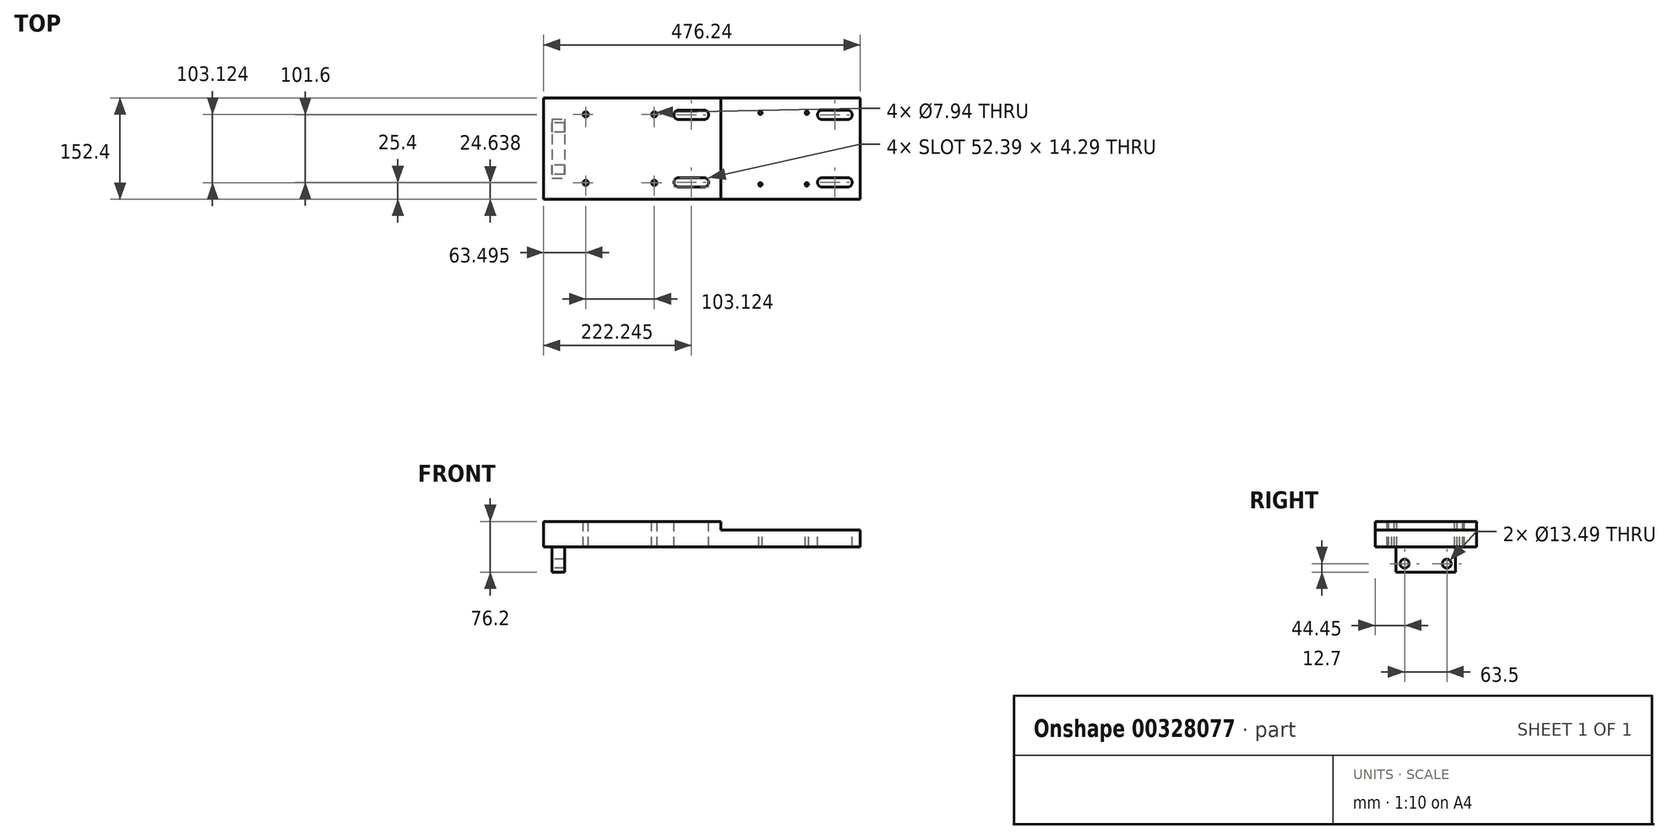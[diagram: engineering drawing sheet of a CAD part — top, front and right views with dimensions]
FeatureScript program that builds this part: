
annotation { "Feature Type Name" : "Feature", "Feature Type Description" : "" }
export const myFeature = defineFeature(function(context is Context, id is Id, definition is map)
    precondition{}
    {
        {
            var Q0;
            Q0=qCreatedBy(makeId("Top.planeOp"),FACE);
            var sketch = newSketch(context, id + "F0", { "sketchPlane" : qUnion([Q0])});
            skLineSegment(sketch, "E0.bottom", {"start": v(-238.13, 76.2) * mm, "end": v(238.13, 76.2) * mm});
            skLineSegment(sketch, "E0.top", {"start": v(-238.13, -76.2) * mm, "end": v(238.12, -76.2) * mm});
            skLineSegment(sketch, "E0.left", {"start": v(-238.13, 76.2) * mm, "end": v(-238.13, -76.2) * mm});
            skLineSegment(sketch, "E0.right", {"start": v(238.13, 76.2) * mm, "end": v(238.12, -76.2) * mm});
            skPoint(sketch, "E0.middle", {"position": v(0, 0) * mm});
            skSolve(sketch);
        }
        {
            var Q0;
            Q0 = qSketchRegion(id + "F0", true);
            extrude(context, id + "F1", {"entities" : qUnion([Q0]), "depth" : 38.1 * mm});
        }
        {
            var Q0;
            Q0=makeQuery(id+"F1.opExtrude","CAP_FACE",FACE,{"disambiguationData":[OSD([sQuery(id+"F0.wireOp",EDGE,"E0.bottom"),sQuery(id+"F0.wireOp",EDGE,"E0.top"),sQuery(id+"F0.wireOp",EDGE,"E0.left"),sQuery(id+"F0.wireOp",EDGE,"E0.right")])],"isStart":false});
            var sketch = newSketch(context, id + "F2", { "sketchPlane" : qUnion([Q0])});
            skPoint(sketch, "E1.0", {"position": v(238.12, -76.2) * mm});
            skLineSegment(sketch, "E2.bottom", {"start": v(238.12, -76.2) * mm, "end": v(28.57, -76.2) * mm});
            skLineSegment(sketch, "E2.top", {"start": v(238.12, 76.2) * mm, "end": v(28.57, 76.2) * mm});
            skLineSegment(sketch, "E2.left", {"start": v(238.12, -76.2) * mm, "end": v(238.12, 76.2) * mm});
            skLineSegment(sketch, "E2.right", {"start": v(28.57, -76.2) * mm, "end": v(28.57, 76.2) * mm});
            skSolve(sketch);
        }
        {
            var Q0;
            Q0 = qSketchRegion(id + "F2", true);
            extrude(context, id + "F3", {"entities" : qUnion([Q0]), "operationType" : NewBodyOperationType.REMOVE, "oppositeDirection" : true, "depth" : 12.7 * mm});
        }
        {
            var Q0;
            Q0=makeQuery(id+"F1.opExtrude","CAP_FACE",FACE,{"disambiguationData":[OSD([sQuery(id+"F0.wireOp",EDGE,"E0.bottom"),sQuery(id+"F0.wireOp",EDGE,"E0.top"),sQuery(id+"F0.wireOp",EDGE,"E0.left"),sQuery(id+"F0.wireOp",EDGE,"E0.right")])],"isStart":false});
            var sketch = newSketch(context, id + "F4", { "sketchPlane" : qUnion([Q0])});
            skLineSegment(sketch, "E3", {"start": v(-358.49, 0) * mm, "end": v(316.47, 0) * mm, "construction": true});
            skLineSegment(sketch, "E4.0", {"start": v(-34.93, 76.2) * mm, "end": v(-34.93, -76.2) * mm, "construction": true});
            skLineSegment(sketch, "E5.0", {"start": v(3.17, 76.2) * mm, "end": v(3.17, -76.2) * mm, "construction": true});
            skLineSegment(sketch, "E6.0", {"start": v(180.97, 76.2) * mm, "end": v(180.97, -76.2) * mm, "construction": true});
            skLineSegment(sketch, "E7.0", {"start": v(219.07, 76.2) * mm, "end": v(219.07, -76.2) * mm, "construction": true});
            skLineSegment(sketch, "E8.0", {"start": v(-358.49, -50.8) * mm, "end": v(316.47, -50.8) * mm, "construction": true});
            skArc(sketch, "E9", {"start": v(-34.93, -43.66) * mm, "mid": v(-42.07, -50.8) * mm, "end": v(-34.93, -57.94) * mm});
            skArc(sketch, "E10", {"start": v(3.17, -57.94) * mm, "mid": v(10.32, -50.8) * mm, "end": v(3.17, -43.66) * mm});
            skArc(sketch, "E11", {"start": v(180.97, -43.66) * mm, "mid": v(173.83, -50.8) * mm, "end": v(180.97, -57.94) * mm});
            skArc(sketch, "E12", {"start": v(219.07, -57.94) * mm, "mid": v(226.22, -50.8) * mm, "end": v(219.07, -43.66) * mm});
            skLineSegment(sketch, "E13", {"start": v(-34.93, -43.66) * mm, "end": v(3.17, -43.66) * mm});
            skLineSegment(sketch, "E14", {"start": v(-34.93, -57.94) * mm, "end": v(3.17, -57.94) * mm});
            skLineSegment(sketch, "E15", {"start": v(180.97, -43.66) * mm, "end": v(219.07, -43.66) * mm});
            skLineSegment(sketch, "E16", {"start": v(180.97, -57.94) * mm, "end": v(219.07, -57.94) * mm});
            skArc(sketch, "E17.MirrorCS", {"start": v(-34.93, 43.66) * mm, "mid": v(-42.07, 50.8) * mm, "end": v(-34.93, 57.94) * mm});
            skArc(sketch, "E18.MirrorCS", {"start": v(3.17, 57.94) * mm, "mid": v(10.32, 50.8) * mm, "end": v(3.17, 43.66) * mm});
            skLineSegment(sketch, "E19.MirrorCS", {"start": v(-34.93, 43.66) * mm, "end": v(3.17, 43.66) * mm});
            skLineSegment(sketch, "E20.MirrorCS", {"start": v(-34.93, 57.94) * mm, "end": v(3.17, 57.94) * mm});
            skLineSegment(sketch, "E21.MirrorCS", {"start": v(180.97, 43.66) * mm, "end": v(219.07, 43.66) * mm});
            skLineSegment(sketch, "E22.MirrorCS", {"start": v(180.97, 57.94) * mm, "end": v(219.07, 57.94) * mm});
            skArc(sketch, "E23.MirrorCS", {"start": v(180.97, 43.66) * mm, "mid": v(173.83, 50.8) * mm, "end": v(180.97, 57.94) * mm});
            skArc(sketch, "E24.MirrorCS", {"start": v(219.07, 57.94) * mm, "mid": v(226.22, 50.8) * mm, "end": v(219.07, 43.66) * mm});
            skSolve(sketch);
        }
        {
            var Q0;
            Q0 = qSketchRegion(id + "F4", true);
            extrude(context, id + "F5", {"entities" : qUnion([Q0]), "operationType" : NewBodyOperationType.REMOVE, "endBound" : BoundingType.THROUGH_ALL, "oppositeDirection" : true, "depth" : 25.4 * mm});
        }
        {
            var Q0;
            Q0=makeQuery(id+"F1.opExtrude","CAP_FACE",FACE,{"disambiguationData":[OSD([sQuery(id+"F0.wireOp",EDGE,"E0.bottom"),sQuery(id+"F0.wireOp",EDGE,"E0.top"),sQuery(id+"F0.wireOp",EDGE,"E0.left"),sQuery(id+"F0.wireOp",EDGE,"E0.right")])],"isStart":false});
            var sketch = newSketch(context, id + "F6", { "sketchPlane" : qUnion([Q0])});
            skLineSegment(sketch, "E25.0", {"start": v(-174.63, 76.2) * mm, "end": v(-174.63, -76.2) * mm, "construction": true});
            skLineSegment(sketch, "E26.0", {"start": v(-71.5, 76.2) * mm, "end": v(-71.5, -76.2) * mm, "construction": true});
            skLineSegment(sketch, "E27", {"start": v(-290.48, 0) * mm, "end": v(301.62, 0) * mm, "construction": true});
            skLineSegment(sketch, "E28.0", {"start": v(-290.48, -51.56) * mm, "end": v(-71.5, -51.56) * mm, "construction": true});
            skPoint(sketch, "E29", {"position": v(-174.63, -51.56) * mm});
            skPoint(sketch, "E30", {"position": v(-71.5, -51.56) * mm});
            skPoint(sketch, "E31.MirrorP", {"position": v(-174.63, 51.56) * mm});
            skPoint(sketch, "E32.MirrorP", {"position": v(-71.5, 51.56) * mm});
            skLineSegment(sketch, "E33.0", {"start": v(88.01, 76.2) * mm, "end": v(88.01, -76.2) * mm, "construction": true});
            skLineSegment(sketch, "E34.0", {"start": v(157.86, 76.2) * mm, "end": v(157.86, -76.2) * mm, "construction": true});
            skLineSegment(sketch, "E35.0", {"start": v(88.01, -53.85) * mm, "end": v(301.62, -53.85) * mm, "construction": true});
            skPoint(sketch, "E36", {"position": v(88.01, -53.85) * mm});
            skPoint(sketch, "E37", {"position": v(157.86, -53.85) * mm});
            skPoint(sketch, "E38.MirrorP", {"position": v(88.01, 53.85) * mm});
            skPoint(sketch, "E39.MirrorP", {"position": v(157.86, 53.85) * mm});
            skSolve(sketch);
        }
        {
            var Q0;
            Q0=sQuery(id+"F6.wireOp",VERTEX,"E31.MirrorP");
            var Q1;
            Q1=sQuery(id+"F6.wireOp",VERTEX,"E32.MirrorP");
            var Q2;
            Q2=sQuery(id+"F6.wireOp",VERTEX,"E29");
            var Q3;
            Q3=sQuery(id+"F6.wireOp",VERTEX,"E30");
            var Q4;
            Q4=makeQuery(id+"F1.opExtrude","SWEPT_BODY",BODY,{"disambiguationData":[OSD([sQuery(id+"F0.wireOp",EDGE,"E0.bottom"),sQuery(id+"F0.wireOp",EDGE,"E0.top"),sQuery(id+"F0.wireOp",EDGE,"E0.left"),sQuery(id+"F0.wireOp",EDGE,"E0.right")])]});
            hole(context, id + "F7", {"style" : HoleStyle.SIMPLE, "endStyle" : HoleEndStyle.THROUGH, "standardTappedOrClearance" : lookupTablePath({ "standard" : "ANSI", "engagement" : "75%", "pitch" : "16 tpi", "size" : "3/8", "type" : "Tapped" }), "standardBlindInLast" : lookupTablePath({ "standard" : "ANSI", "engagement" : "75%", "pitch" : "16 tpi", "size" : "3/8", "type" : "Tapped" }), "holeDiameter" : 7.94 * mm, "showTappedDepth" : true, "tappedDepth" : 12.06 * mm, "tapClearance" : 3, "locations" : qUnion([Q0, Q1, Q2, Q3]), "scope" : qUnion([Q4]), "majorDiameter" : 9.53 * mm});
        }
        {
            var Q0;
            Q0=sQuery(id+"F6.wireOp",VERTEX,"E38.MirrorP");
            var Q1;
            Q1=sQuery(id+"F6.wireOp",VERTEX,"E39.MirrorP");
            var Q2;
            Q2=sQuery(id+"F6.wireOp",VERTEX,"E36");
            var Q3;
            Q3=sQuery(id+"F6.wireOp",VERTEX,"E37");
            var Q4;
            Q4=makeQuery(id+"F1.opExtrude","SWEPT_BODY",BODY,{"disambiguationData":[OSD([sQuery(id+"F0.wireOp",EDGE,"E0.bottom"),sQuery(id+"F0.wireOp",EDGE,"E0.top"),sQuery(id+"F0.wireOp",EDGE,"E0.left"),sQuery(id+"F0.wireOp",EDGE,"E0.right")])]});
            hole(context, id + "F8", {"style" : HoleStyle.SIMPLE, "endStyle" : HoleEndStyle.THROUGH, "standardTappedOrClearance" : lookupTablePath({ "standard" : "ANSI", "engagement" : "75%", "pitch" : "20 tpi", "size" : "1/4", "type" : "Tapped" }), "standardBlindInLast" : lookupTablePath({ "standard" : "ANSI", "engagement" : "75%", "pitch" : "20 tpi", "size" : "1/4", "type" : "Tapped" }), "holeDiameter" : 5.1 * mm, "showTappedDepth" : true, "tappedDepth" : 12.06 * mm, "tapClearance" : 3, "locations" : qUnion([Q0, Q1, Q2, Q3]), "scope" : qUnion([Q4]), "majorDiameter" : 6.35 * mm});
        }
        {
            var Q0;
            Q0=makeQuery(id+"F1.opExtrude","CAP_FACE",FACE,{"disambiguationData":[OSD([sQuery(id+"F0.wireOp",EDGE,"E0.bottom"),sQuery(id+"F0.wireOp",EDGE,"E0.top"),sQuery(id+"F0.wireOp",EDGE,"E0.left"),sQuery(id+"F0.wireOp",EDGE,"E0.right")])],"isStart":true});
            var sketch = newSketch(context, id + "F9", { "sketchPlane" : qUnion([Q0])});
            skLineSegment(sketch, "E40.0", {"start": v(-225.43, -76.2) * mm, "end": v(-225.43, 76.2) * mm, "construction": true});
            skLineSegment(sketch, "E41.0", {"start": v(-290.48, -44.45) * mm, "end": v(301.62, -44.45) * mm, "construction": true});
            skLineSegment(sketch, "E42.bottom", {"start": v(-225.43, -44.45) * mm, "end": v(-206.38, -44.45) * mm});
            skLineSegment(sketch, "E42.top", {"start": v(-225.43, 44.45) * mm, "end": v(-206.38, 44.45) * mm});
            skLineSegment(sketch, "E42.left", {"start": v(-225.43, -44.45) * mm, "end": v(-225.43, 44.45) * mm});
            skLineSegment(sketch, "E42.right", {"start": v(-206.38, -44.45) * mm, "end": v(-206.38, 44.45) * mm});
            skSolve(sketch);
        }
        {
            var Q0;
            Q0 = qSketchRegion(id + "F9", true);
            extrude(context, id + "F10", {"entities" : qUnion([Q0]), "operationType" : NewBodyOperationType.ADD, "depth" : 38.1 * mm});
        }
        {
            var Q0;
            Q0=makeQuery(id+"F10.opExtrude","SWEPT_FACE",FACE,{"disambiguationData":[OSD([sQuery(id+"F9.wireOp",EDGE,"E42.left")])]});
            var sketch = newSketch(context, id + "F11", { "sketchPlane" : qUnion([Q0])});
            skLineSegment(sketch, "E43.0", {"start": v(-76.2, -25.4) * mm, "end": v(76.2, -25.4) * mm, "construction": true});
            skLineSegment(sketch, "E44.0", {"start": v(-31.75, -38.1) * mm, "end": v(-31.75, 0) * mm, "construction": true});
            skLineSegment(sketch, "E45.0", {"start": v(31.75, -38.1) * mm, "end": v(31.75, 0) * mm, "construction": true});
            skPoint(sketch, "E46", {"position": v(-31.75, -25.4) * mm});
            skPoint(sketch, "E47", {"position": v(31.75, -25.4) * mm});
            skSolve(sketch);
        }
        {
            var Q0;
            Q0=sQuery(id+"F11.wireOp",VERTEX,"E46");
            var Q1;
            Q1=sQuery(id+"F11.wireOp",VERTEX,"E47");
            var Q2;
            Q2=makeQuery(id+"F1.opExtrude","SWEPT_BODY",BODY,{"disambiguationData":[OSD([sQuery(id+"F0.wireOp",EDGE,"E0.bottom"),sQuery(id+"F0.wireOp",EDGE,"E0.top"),sQuery(id+"F0.wireOp",EDGE,"E0.left"),sQuery(id+"F0.wireOp",EDGE,"E0.right")])]});
            hole(context, id + "F12", {"style" : HoleStyle.SIMPLE, "endStyle" : HoleEndStyle.THROUGH, "standardTappedOrClearance" : lookupTablePath({ "standard" : "ANSI", "engagement" : "75%", "pitch" : "11 tpi", "size" : "5/8", "type" : "Tapped" }), "standardBlindInLast" : lookupTablePath({ "standard" : "ANSI", "engagement" : "75%", "pitch" : "11 tpi", "size" : "5/8", "type" : "Tapped" }), "holeDiameter" : 13.5 * mm, "showTappedDepth" : true, "tappedDepth" : 12.06 * mm, "tapClearance" : 3, "locations" : qUnion([Q0, Q1]), "scope" : qUnion([Q2]), "majorDiameter" : 15.88 * mm});
        }
    });
